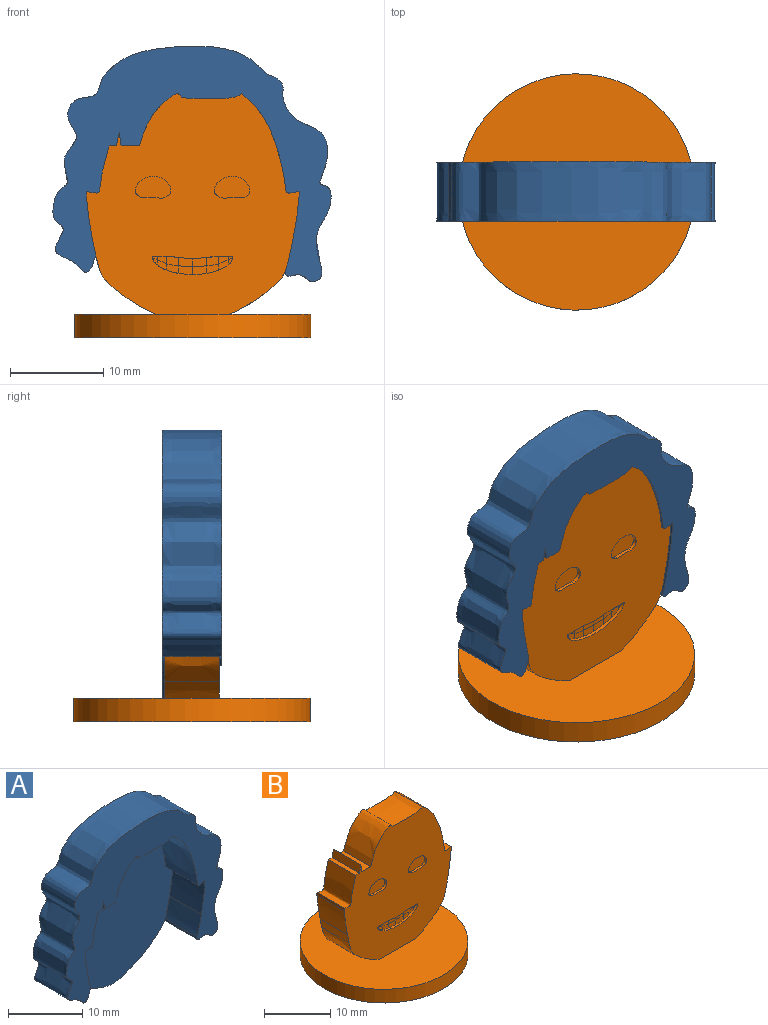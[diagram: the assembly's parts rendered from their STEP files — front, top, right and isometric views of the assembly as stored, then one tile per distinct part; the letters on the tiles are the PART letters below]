
ASSEMBLY  parts=2 mates=1
PART A: 23 faces, bbox 30.2x6.4x30.1 mm
  f0: extruded ~6.45x6.1mm, area 39.9mm2, adj f1,f14,f15,f20
  f1: extruded ~10.66x6.18mm, area 81.3mm2, adj f0,f2,f15,f20
  f2: extruded ~6.1x0.48mm, area 3mm2, adj f1,f3,f15,f20
  f3: extruded ~6.1x4.73mm, area 29.2mm2, adj f2,f4,f15,f20
  f4: extruded ~6.1x3.34mm, area 21mm2, adj f3,f5,f15,f20
  f5: extruded ~29.43x25.05mm, area 495.8mm2, adj f4,f6,f15,f16,f19,f22
  f6: extruded ~6.1x1.71mm, area 10.6mm2, adj f5,f7,f15,f20
  f7: extruded ~6.1x4.73mm, area 29.2mm2, adj f6,f8,f15,f20
  f8: extruded ~6.1x0.48mm, area 3mm2, adj f7,f9,f15,f20
  f9: extruded ~6.1x5.05mm, area 39.4mm2, adj f8,f10,f15,f20
  f10: plane 6.1x0.79mm, normal (0,0,-1), area 4.8mm2, adj f9,f11,f15,f20
  f11: plane 6.1x1.42mm, normal (0.98,0,-0.21), area 8.9mm2, adj f10,f12,f15,f20
  f12: plane 6.1x1.42mm, normal (-0.99,0,-0.13), area 8.7mm2, adj f11,f13,f15,f20
  f13: plane 6.1x1.97mm, normal (0,0,-1), area 12mm2, adj f12,f14,f15,f20
  f14: extruded ~6.1x5.6mm, area 48mm2, adj f0,f13,f15,f20
  f15: plane 30.21x25.68mm, normal (0,-1,0), area 252.7mm2, adj f0,f1,f2,f3,f4,f5,f6,f7
  f16: plane 30.21x30.11mm, normal (0,1,0), area 672.4mm2, adj f5,f17,f18,f19,f21,f22
  f17: cylinder r=5.08mm len=2.73mm, axis (0,-1,0), area 0.7mm2, adj f16,f18,f20,f21
  f18: extruded ~5.8x2.76mm, area 1.6mm2, adj f16,f17,f19,f20
  f19: extruded ~4.44x3.23mm, area 1.4mm2, adj f5,f16,f18,f20
  f20: plane 24.94x22.86mm, normal (0,-1,0), area 419.7mm2, adj f0,f1,f2,f3,f4,f6,f7,f8
  f21: extruded ~5.8x2.76mm, area 1.6mm2, adj f16,f17,f20,f22
  f22: extruded ~2.81x2.77mm, area 1mm2, adj f5,f16,f20,f21
PART B: 52 faces, bbox 25.4x25.4x26.4 mm
  f0: extruded ~5.84x3.19mm, area 21.5mm2, adj f2,f3,f21,f50
  f1: extruded ~5.84x3.19mm, area 21.5mm2, adj f2,f3,f22,f50
  f2: plane 23.82x22.86mm, normal (0,-1,0), area 387.4mm2, adj f0,f1,f19,f20,f21,f22,f23,f24
  f3: plane 23.82x22.86mm, normal (0,1,0), area 414.1mm2, adj f0,f1,f19,f20,f21,f22,f23,f24
  f4: plane 0.8x0.5mm, normal (0,-1,0), area 0.2mm2, adj f5,f7,f34
  f5: plane 0.51x0.34mm, normal (0,-1,0), area 0.1mm2, adj f4,f6,f34,f42
  f6: plane 1.03x0.78mm, normal (0,-1,0), area 0.6mm2, adj f5,f7,f8,f42
  f7: plane 1.14x1.03mm, normal (0,-1,0), area 0.7mm2, adj f4,f6,f9,f34
  f8: plane 1.28x1.01mm, normal (0,-1,0), area 1.1mm2, adj f6,f9,f11,f42
  f9: plane 1.28x1.04mm, normal (0,-1,0), area 1mm2, adj f7,f8,f10,f34
  f10: plane 1.53x0.93mm, normal (0,-1,0), area 1.3mm2, adj f9,f11,f18,f34
  f11: plane 1.53x0.99mm, normal (0,-1,0), area 1.3mm2, adj f8,f10,f12,f42
  f12: plane 1.53x0.99mm, normal (0,-1,0), area 1.3mm2, adj f11,f14,f18,f35
  f13: plane 1.03x0.78mm, normal (0,-1,0), area 0.6mm2, adj f14,f15,f16,f35
  f14: plane 1.28x1.01mm, normal (0,-1,0), area 1.1mm2, adj f12,f13,f17,f35
  f15: plane 0.51x0.34mm, normal (0,-1,0), area 0.1mm2, adj f13,f34,f35,f48
  f16: plane 1.14x1.03mm, normal (0,-1,0), area 0.7mm2, adj f13,f17,f34,f48
  f17: plane 1.28x1.04mm, normal (0,-1,0), area 1mm2, adj f14,f16,f18,f34
  f18: plane 1.53x0.93mm, normal (0,-1,0), area 1.3mm2, adj f10,f12,f17,f34
  f19: extruded ~5.84x4.73mm, area 27.9mm2, adj f2,f3,f20,f45
  f20: extruded ~5.84x1.71mm, area 10.2mm2, adj f2,f3,f19,f21
  f21: extruded ~5.84x4.44mm, area 33.3mm2, adj f0,f2,f3,f20
  f22: extruded ~5.84x2.81mm, area 23.4mm2, adj f1,f2,f3,f23
  f23: extruded ~5.84x3.34mm, area 20.1mm2, adj f2,f3,f22,f24
  f24: extruded ~5.84x4.73mm, area 27.9mm2, adj f2,f3,f23,f25
  f25: extruded ~5.84x0.48mm, area 2.8mm2, adj f2,f3,f24,f26
  f26: extruded ~10.66x6.18mm, area 77.9mm2, adj f2,f3,f25,f27
  f27: extruded ~6.45x5.84mm, area 38.3mm2, adj f2,f3,f26,f28
  f28: extruded ~5.84x5.6mm, area 46mm2, adj f2,f3,f27,f29
  f29: plane 5.84x1.97mm, normal (0,0,1), area 11.5mm2, adj f2,f3,f28,f30
  f30: plane 5.84x1.42mm, normal (0.99,0,0.13), area 8.4mm2, adj f2,f3,f29,f31
  f31: plane 5.84x1.42mm, normal (-0.98,0,0.21), area 8.5mm2, adj f2,f3,f30,f32
  f32: plane 5.84x0.79mm, normal (0,0,1), area 4.6mm2, adj f2,f3,f31,f33
  f33: extruded ~5.84x5.05mm, area 37.8mm2, adj f2,f3,f32,f45
  f34: extruded ~8.64x1.91mm, area 3.9mm2, adj f2,f4,f5,f7,f9,f10,f15,f16
  f35: extruded ~4.32x0.38mm, area 1.7mm2, adj f2,f12,f13,f14,f15,f34,f42
  f36: extruded ~0.77x0.72mm, area 0.4mm2, adj f2,f37,f43,f47
  f37: extruded ~2.11x0.38mm, area 0.8mm2, adj f2,f36,f38,f47
  f38: extruded ~0.93x0.76mm, area 0.5mm2, adj f2,f37,f43,f47
  f39: extruded ~0.93x0.76mm, area 0.5mm2, adj f2,f40,f44,f46
  f40: extruded ~2.11x0.38mm, area 0.8mm2, adj f2,f39,f41,f46
  f41: extruded ~0.77x0.72mm, area 0.4mm2, adj f2,f40,f44,f46
  f42: extruded ~4.32x0.38mm, area 1.7mm2, adj f2,f5,f6,f8,f11,f34,f35
  f43: extruded ~3.81x1.59mm, area 2.1mm2, adj f2,f36,f38,f47
  f44: extruded ~3.81x1.59mm, area 2.1mm2, adj f2,f39,f41,f46
  f45: extruded ~5.84x0.48mm, area 2.8mm2, adj f2,f3,f19,f33
  f46: plane 3.81x2.35mm, normal (0,-1,0), area 7.1mm2, adj f39,f40,f41,f44
  f47: plane 3.81x2.35mm, normal (0,-1,0), area 7.1mm2, adj f36,f37,f38,f43
  f48: plane 0.8x0.5mm, normal (0,-1,0), area 0.2mm2, adj f15,f16,f34
  f49: cylinder r=12.7mm len=25.4mm, axis (0,0,1), area 202.7mm2, adj f50,f51
  f50: plane 25.4x25.4mm, normal (0,0,1), area 460.3mm2, adj f0,f1,f2,f3,f49
  f51: plane 25.4x25.4mm, normal (0,0,-1), area 506.7mm2, adj f49
PLACE A t=(0,0,1.27)mm
PLACE B t=(0,0,1.27)mm
MATE fastened A.f20 <-> B.f3  axis (0,-1,0) through (2.09,2.92,25.72)mm
